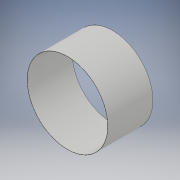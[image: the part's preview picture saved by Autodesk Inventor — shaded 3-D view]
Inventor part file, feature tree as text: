
AUTODESK INVENTOR PART (.ipt)
format: ipt  version: 2019 (Build 230136000, 136)  size: 103,424 bytes
history: native  units: mm
features: extrude x2, sketch x2
ambient origin geometry x8: Origin, YZ Plane, XZ Plane, XY Plane, X Axis, Y Axis, Z Axis, Center Point
bodies: Solid1 (feature_tree)
feature tree (4):
  extrude  "Extrusion1"  Depth=113.5mm TaperAngle=0.0deg
  extrude  "Extrusion2"  Depth=11.35mm TaperAngle=0.0deg
  sketch  "Sketch1"  dims[d0=203.7mm d1=113.5mm d2=0.0mm]
  sketch  "Sketch2"  dims[d3=202.7mm d4=11.35mm d5=0.0mm]
